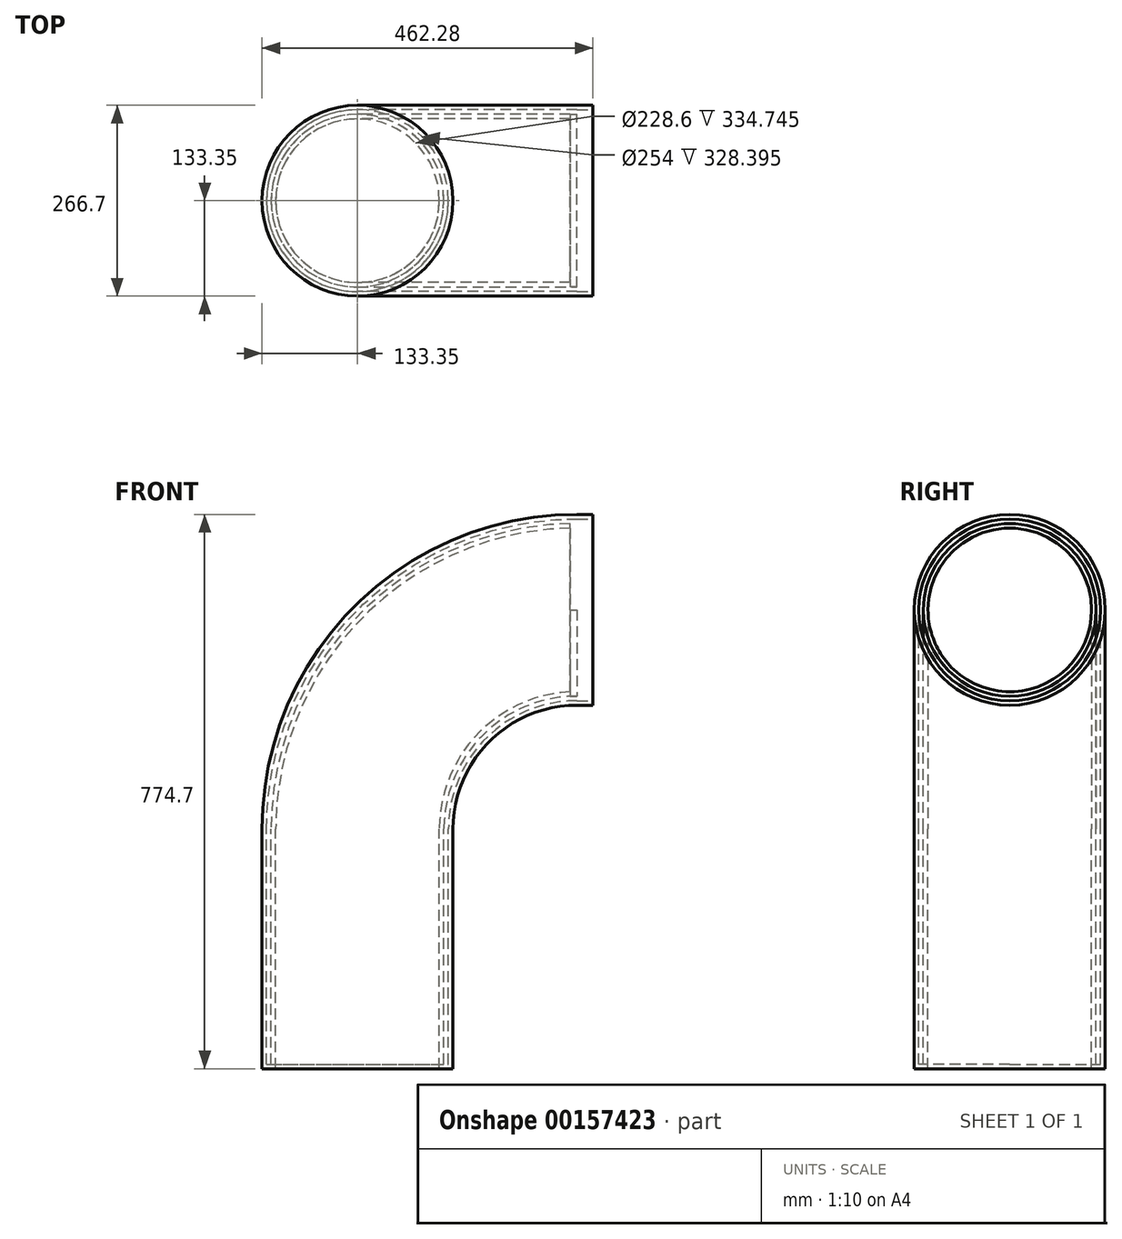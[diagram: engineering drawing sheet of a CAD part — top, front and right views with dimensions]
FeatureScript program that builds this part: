
annotation { "Feature Type Name" : "Feature", "Feature Type Description" : "" }
export const myFeature = defineFeature(function(context is Context, id is Id, definition is map)
    precondition{}
    {
        {
            var Q0;
            Q0=qCreatedBy(makeId("Front.planeOp"),FACE);
            var sketch = newSketch(context, id + "F0", { "sketchPlane" : qUnion([Q0])});
            skLineSegment(sketch, "E0.bottom", {"start": v(0, 0) * mm, "end": v(-254, 0) * mm});
            skLineSegment(sketch, "E0.left", {"start": v(0, 0) * mm, "end": v(0, 328.4) * mm});
            skLineSegment(sketch, "E0.right", {"start": v(-254, 0) * mm, "end": v(-254, 328.4) * mm});
            skLineSegment(sketch, "E1.bottom", {"start": v(179.6, 762) * mm, "end": v(201.93, 762) * mm});
            skLineSegment(sketch, "E1.top", {"start": v(179.6, 508) * mm, "end": v(201.93, 508) * mm});
            skArc(sketch, "E2", {"start": v(179.6, 508) * mm, "mid": v(52.6, 455.4) * mm, "end": v(0, 328.4) * mm});
            skArc(sketch, "E3", {"start": v(179.6, 762) * mm, "mid": v(-127, 635) * mm, "end": v(-254, 328.4) * mm});
            skLineSegment(sketch, "E4", {"start": v(201.93, 508) * mm, "end": v(201.93, 762) * mm});
            skSolve(sketch);
        }
        {
            var Q0;
            Q0=qSketchRegion(id+"F0",true);
            extrude(context, id + "F1", {"entities" : qUnion([Q0]), "depth" : 254 * mm});
        }
        {
            var Q0;
            Q0=makeQuery(id+"F1.opExtrude","CAP_EDGE",EDGE,{"disambiguationData":[OSD([sQuery(id+"F0.wireOp",EDGE,"E1.top")])],"isStart":false});
            var Q1;
            Q1=makeQuery(id+"F1.opExtrude","CAP_EDGE",EDGE,{"disambiguationData":[OSD([sQuery(id+"F0.wireOp",EDGE,"E3")])],"isStart":false});
            var Q2;
            Q2=makeQuery(id+"F1.opExtrude","CAP_EDGE",EDGE,{"disambiguationData":[OSD([sQuery(id+"F0.wireOp",EDGE,"E3")])],"isStart":true});
            var Q3;
            Q3=makeQuery(id+"F1.opExtrude","CAP_EDGE",EDGE,{"disambiguationData":[OSD([sQuery(id+"F0.wireOp",EDGE,"E2")])],"isStart":true});
            fillet(context, id + "F2", {"entities" : qUnion([Q0, Q1, Q2, Q3]), "radius" : 127 * mm, "tangentPropagation" : true, "allowEdgeOverflow" : false});
        }
        {
            var Q0;
            Q0=makeQuery(id+"F1.opExtrude","SWEPT_FACE",FACE,{"disambiguationData":[OSD([sQuery(id+"F0.wireOp",EDGE,"E0.bottom")])]});
            var Q1;
            Q1=makeQuery(id+"F1.opExtrude","SWEPT_FACE",FACE,{"disambiguationData":[OSD([sQuery(id+"F0.wireOp",EDGE,"E1.right")])]});
            shell(context, id + "F3", {"entities" : qUnion([Q0, Q1]), "thickness" : 6.35 * mm});
        }
        {
            var Q0;
            Q0=makeQuery(id+"F1.opExtrude","SWEPT_FACE",FACE,{"disambiguationData":[OSD([sQuery(id+"F0.wireOp",EDGE,"E4")])]});
            shell(context, id + "F4", {"entities" : qUnion([Q0]), "thickness" : 6.35 * mm, "oppositeDirection" : true});
        }
        {
            var Q0;
            Q0=makeQuery(id+"F4.opShell","OFFSET_FACE",FACE,{"disambiguationData":[OSD([sQuery(id+"F0.wireOp",EDGE,"E4")])]});
            extrude(context, id + "F5", {"entities" : qUnion([Q0]), "operationType" : NewBodyOperationType.REMOVE, "oppositeDirection" : true, "depth" : 25.4 * mm});
        }
    });
